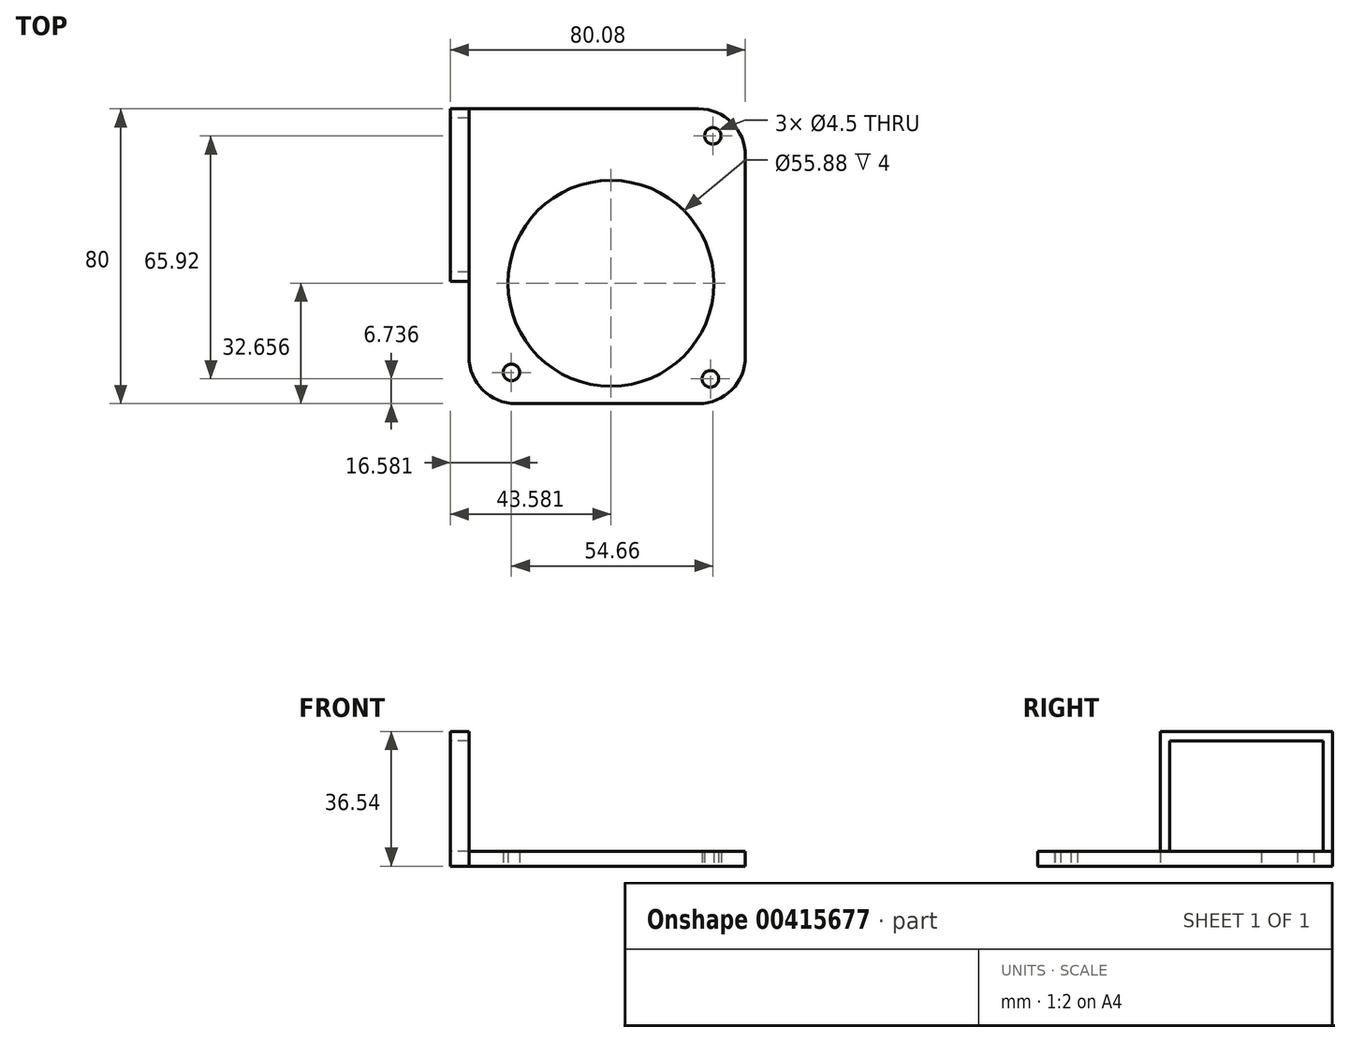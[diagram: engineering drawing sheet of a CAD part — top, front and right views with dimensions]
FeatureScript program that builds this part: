
annotation { "Feature Type Name" : "Feature", "Feature Type Description" : "" }
export const myFeature = defineFeature(function(context is Context, id is Id, definition is map)
    precondition{}
    {
        {
            assignVariable(context, id + "F0", {"name" : "thickness", "anyValue" : 4 * mm});
        }
        {
            var Q0;
            Q0=qCreatedBy(makeId("Top.planeOp"),FACE);
            var sketch = newSketch(context, id + "F1", { "sketchPlane" : qUnion([Q0])});
            skLineSegment(sketch, "E0.bottom", {"start": v(-55.38, 44) * mm, "end": v(6.92, 44) * mm});
            skLineSegment(sketch, "E0.top", {"start": v(-42.68, -36) * mm, "end": v(6.92, -36) * mm});
            skLineSegment(sketch, "E0.left", {"start": v(-55.38, 44) * mm, "end": v(-55.38, -23.3) * mm});
            skLineSegment(sketch, "E0.right", {"start": v(19.62, 31.3) * mm, "end": v(19.62, -23.3) * mm});
            skCircle(sketch, "E1", {"center": v(10.78, 36.66) * mm, "radius": 2.25 * mm});
            skLineSegment(sketch, "E2", {"start": v(-16.88, 52.33) * mm, "end": v(-16.88, -42.92) * mm});
            skLineSegment(sketch, "E3", {"start": v(-77.65, -3.34) * mm, "end": v(41.37, -3.34) * mm});
            skCircle(sketch, "E4", {"center": v(10.12, -29.26) * mm, "radius": 2.25 * mm});
            skCircle(sketch, "E5", {"center": v(-43.88, -27.55) * mm, "radius": 2.25 * mm});
            skPoint(sketch, "E6.visualSharp", {"position": v(19.62, -36) * mm});
            skArc(sketch, "E6.filletArc", {"start": v(6.92, -36) * mm, "mid": v(15.9, -32.28) * mm, "end": v(19.62, -23.3) * mm});
            skPoint(sketch, "E7.visualSharp", {"position": v(-55.38, -36) * mm});
            skArc(sketch, "E7.filletArc", {"start": v(-55.38, -23.3) * mm, "mid": v(-51.66, -32.28) * mm, "end": v(-42.68, -36) * mm});
            skPoint(sketch, "E8.visualSharp", {"position": v(19.62, 44) * mm});
            skArc(sketch, "E8.filletArc", {"start": v(19.62, 31.3) * mm, "mid": v(15.9, 40.28) * mm, "end": v(6.92, 44) * mm});
            skCircle(sketch, "E9", {"center": v(-16.88, -3.34) * mm, "radius": 27.94 * mm});
            skSolve(sketch);
        }
        {
            var Q0;
            Q0=makeQuery(id+"F1.imprint","IMPRINT",FACE,{"disambiguationData":[TD([[makeQuery(id+"F1.imprint","IMPRINT",EDGE,{"derivedFrom":sQuery(id+"F1.wireOp",EDGE,"E1")}),-1.0]])]});
            var Q1;
            Q1=makeQuery(id+"F1.imprint","IMPRINT",FACE,{"disambiguationData":[TD([[makeQuery(id+"F1.imprint","IMPRINT",EDGE,{"derivedFrom":sQuery(id+"F1.wireOp",EDGE,"E4")}),-1.0]])]});
            var Q2;
            Q2=makeQuery(id+"F1.imprint","IMPRINT",FACE,{"disambiguationData":[TD([[makeQuery(id+"F1.imprint","IMPRINT",EDGE,{"derivedFrom":sQuery(id+"F1.wireOp",EDGE,"E5")}),-1.0]])]});
            var Q3;
            {var subQ0=sQuery(id+"F1.wireOp",EDGE,"E0.left");var subQ1=sQuery(id+"F1.wireOp",EDGE,"E0.bottom");var subQ2=makeQuery(id+"F1.imprint","INTERSECT",VERTEX,{"derivedFrom":[subQ1,subQ0]});Q3=makeQuery(id+"F1.imprint","IMPRINT",FACE,{"disambiguationData":[TD([[makeQuery(id+"F1.imprint","IMPRINT",EDGE,{"disambiguationData":[TD([[subQ2,-1.0]])],"derivedFrom":subQ1}),-1.0]])]});}
            extrude(context, id + "F2", {"entities" : qUnion([Q0, Q1, Q2, Q3]), "depth" : getVariable(context, 'thickness')});
        }
        {
            var Q0;
            Q0=makeQuery(id+"F2.opExtrude","SWEPT_FACE",FACE,{"disambiguationData":[OSD([sQuery(id+"F1.wireOp",EDGE,"E0.left")])]});
            var sketch = newSketch(context, id + "F3", { "sketchPlane" : qUnion([Q0])});
            skLineSegment(sketch, "E10.bottom", {"start": v(2.78, 36.54) * mm, "end": v(-44, 36.54) * mm});
            skLineSegment(sketch, "E10.top", {"start": v(2.78, 0) * mm, "end": v(-44, 0) * mm});
            skLineSegment(sketch, "E10.left", {"start": v(2.78, 36.54) * mm, "end": v(2.78, 0) * mm});
            skLineSegment(sketch, "E10.right", {"start": v(-44, 36.54) * mm, "end": v(-44, 0) * mm});
            skPoint(sketch, "E11.endSnap0", {"position": v(-20.6, 0) * mm});
            skLineSegment(sketch, "E12", {"start": v(-20.6, 36.54) * mm, "end": v(-20.6, 0) * mm, "construction": true});
            skLineSegment(sketch, "E13", {"start": v(-44, 18.27) * mm, "end": v(2.78, 18.27) * mm, "construction": true});
            skSolve(sketch);
        }
        {
            var Q0;
            {var subQ0=sQuery(id+"F3.wireOp",EDGE,"E10.top");Q0=makeQuery(id+"F3.imprint","IMPRINT",FACE,{"disambiguationData":[TD([[makeQuery(id+"F3.imprint","IMPRINT",EDGE,{"derivedFrom":subQ0}),1.0]])]});}
            var Q1;
            {var subQ0=sQuery(id+"F3.wireOp",EDGE,"E10.bottom");Q1=makeQuery(id+"F3.imprint","IMPRINT",FACE,{"disambiguationData":[TD([[makeQuery(id+"F3.imprint","IMPRINT",EDGE,{"derivedFrom":subQ0}),1.0]])]});}
            extrude(context, id + "F4", {"entities" : qUnion([Q0, Q1]), "operationType" : NewBodyOperationType.ADD, "depth" : 5.08 * mm});
        }
        {
            var Q0;
            Q0=makeQuery(id+"F4.opExtrude","CAP_FACE",FACE,{"disambiguationData":[OSD([sQuery(id+"F3.wireOp",EDGE,"E10.bottom"),sQuery(id+"F3.wireOp",EDGE,"E10.top"),sQuery(id+"F3.wireOp",EDGE,"E10.left"),sQuery(id+"F3.wireOp",EDGE,"E10.right")])],"isStart":false});
            var sketch = newSketch(context, id + "F5", { "sketchPlane" : qUnion([Q0])});
            skLineSegment(sketch, "E14.bottom", {"start": v(-41.46, 34) * mm, "end": v(0.24, 34) * mm});
            skLineSegment(sketch, "E14.top", {"start": v(-41.46, 4) * mm, "end": v(0.24, 4) * mm});
            skLineSegment(sketch, "E14.left", {"start": v(-41.46, 34) * mm, "end": v(-41.46, 4) * mm});
            skLineSegment(sketch, "E14.right", {"start": v(0.24, 34) * mm, "end": v(0.24, 4) * mm});
            skSolve(sketch);
        }
        {
            var Q0;
            Q0=qSketchRegion(id+"F5",true);
            extrude(context, id + "F6", {"entities" : qUnion([Q0]), "operationType" : NewBodyOperationType.REMOVE, "oppositeDirection" : true, "depth" : 25.4 * mm});
        }
    });
